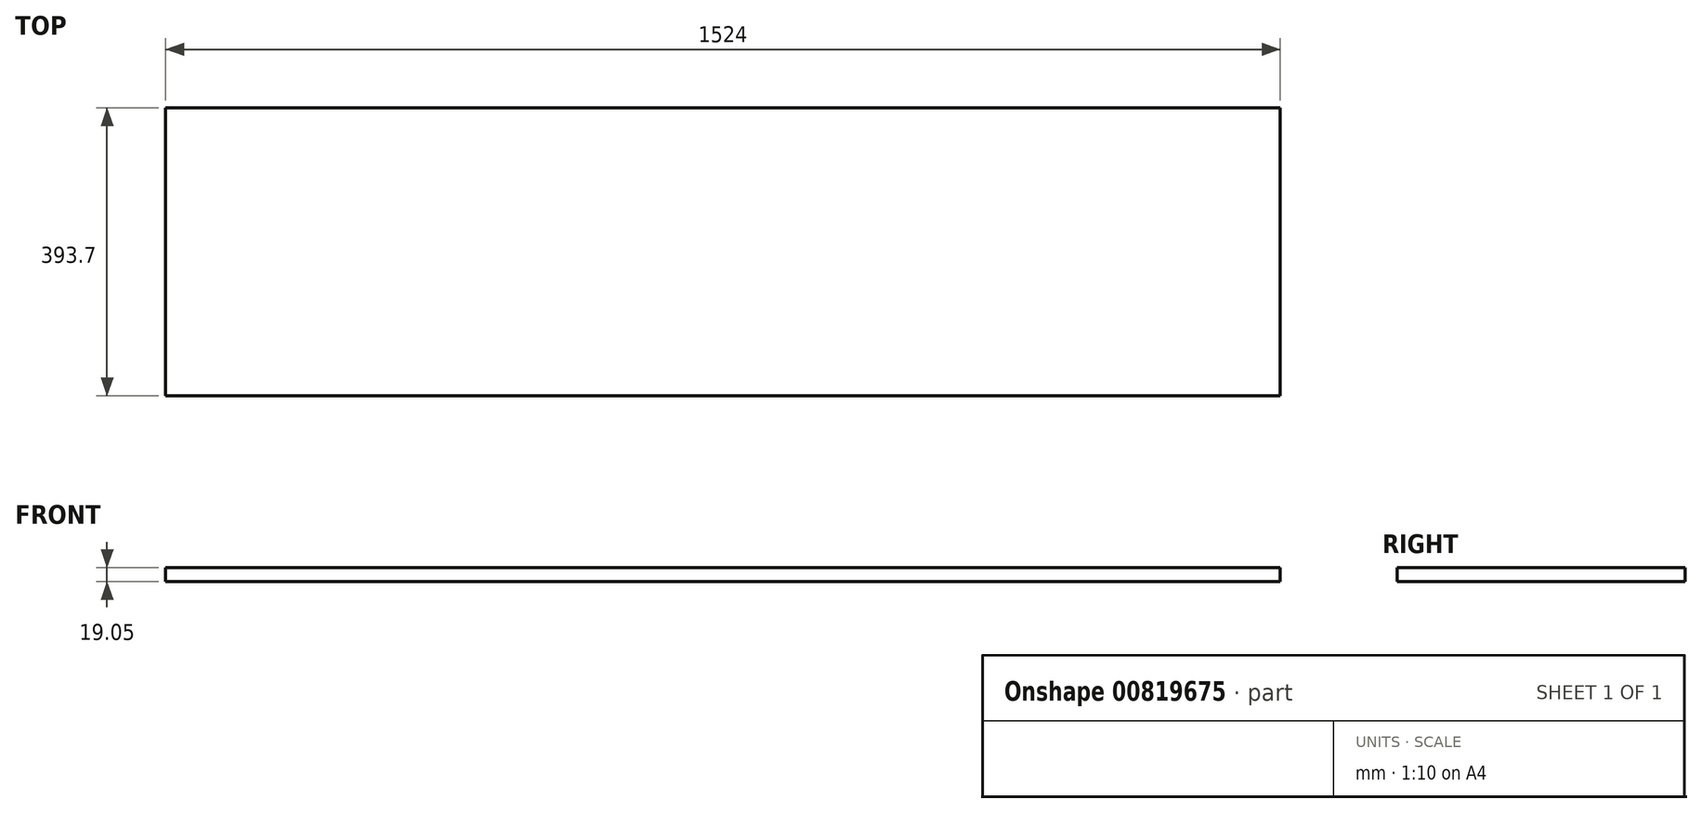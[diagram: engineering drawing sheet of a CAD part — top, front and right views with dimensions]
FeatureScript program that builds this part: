
annotation { "Feature Type Name" : "Feature", "Feature Type Description" : "" }
export const myFeature = defineFeature(function(context is Context, id is Id, definition is map)
    precondition{}
    {
        {
            var Q0;
            Q0=qCreatedBy(makeId("Front.planeOp"),FACE);
            var sketch = newSketch(context, id + "F0", { "sketchPlane" : qUnion([Q0])});
            skLineSegment(sketch, "E0.bottom", {"start": v(1457.83, 0) * mm, "end": v(-66.17, 0) * mm});
            skLineSegment(sketch, "E0.top", {"start": v(1457.83, 19.05) * mm, "end": v(-66.17, 19.05) * mm});
            skLineSegment(sketch, "E0.left", {"start": v(1457.83, 0) * mm, "end": v(1457.83, 19.05) * mm});
            skLineSegment(sketch, "E0.right", {"start": v(-66.17, 0) * mm, "end": v(-66.17, 19.05) * mm});
            skSolve(sketch);
        }
        {
            var Q0;
            Q0=makeQuery(id+"F0.imprint","IMPRINT",FACE,{"disambiguationData":[TD([[makeQuery(id+"F0.imprint","IMPRINT",EDGE,{"derivedFrom":sQuery(id+"F0.wireOp",EDGE,"E0.bottom")}),-1.0]])]});
            extrude(context, id + "F1", {"entities" : qUnion([Q0]), "depth" : 393.7 * mm, "offsetDistance" : 25.4 * mm});
        }
    });
